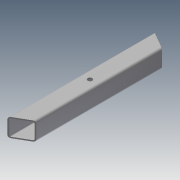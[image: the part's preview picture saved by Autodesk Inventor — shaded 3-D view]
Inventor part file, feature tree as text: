
AUTODESK INVENTOR PART (.ipt)
format: ipt  version: 2013 SP2 (Build 170200200, 200)  size: 118,272 bytes
history: native  units: in
note: dims shown in document units (in); Inventor stores cm internally (conversion verified against a paired STEP export)
features: sketch x3, extrude x2, hole x1
ambient origin geometry x8: Origin, YZ Plane, XZ Plane, XY Plane, X Axis, Y Axis, Z Axis, Center Point
bodies: Solid1 (feature_tree)
feature tree (6):
  extrude  "Extrusion1"  Depth=1.0in
  extrude  "Extrusion2"  Depth=0.065in
  hole  "Hole1"  [1 undecoded]
  sketch  "Sketch1"  dims[d0=1.0in d1=1.0in]
  sketch  "Sketch2"  dims[d2=0.125in d3=0.065in]
  sketch  "Sketch3"  dims[d4=8.0in d5=0.0in d10=8.0in d11=0.0in d12=0.25in d13=0.75in d14=0.375in d15=0.25in d16=0.5635in d17=1.0in d18=0.8108in]
note: 1 required parameter value undecoded (feature->parameter linkage not recoverable at this tier; creation-order binding heuristic only, values carry confidence <= 0.55)
